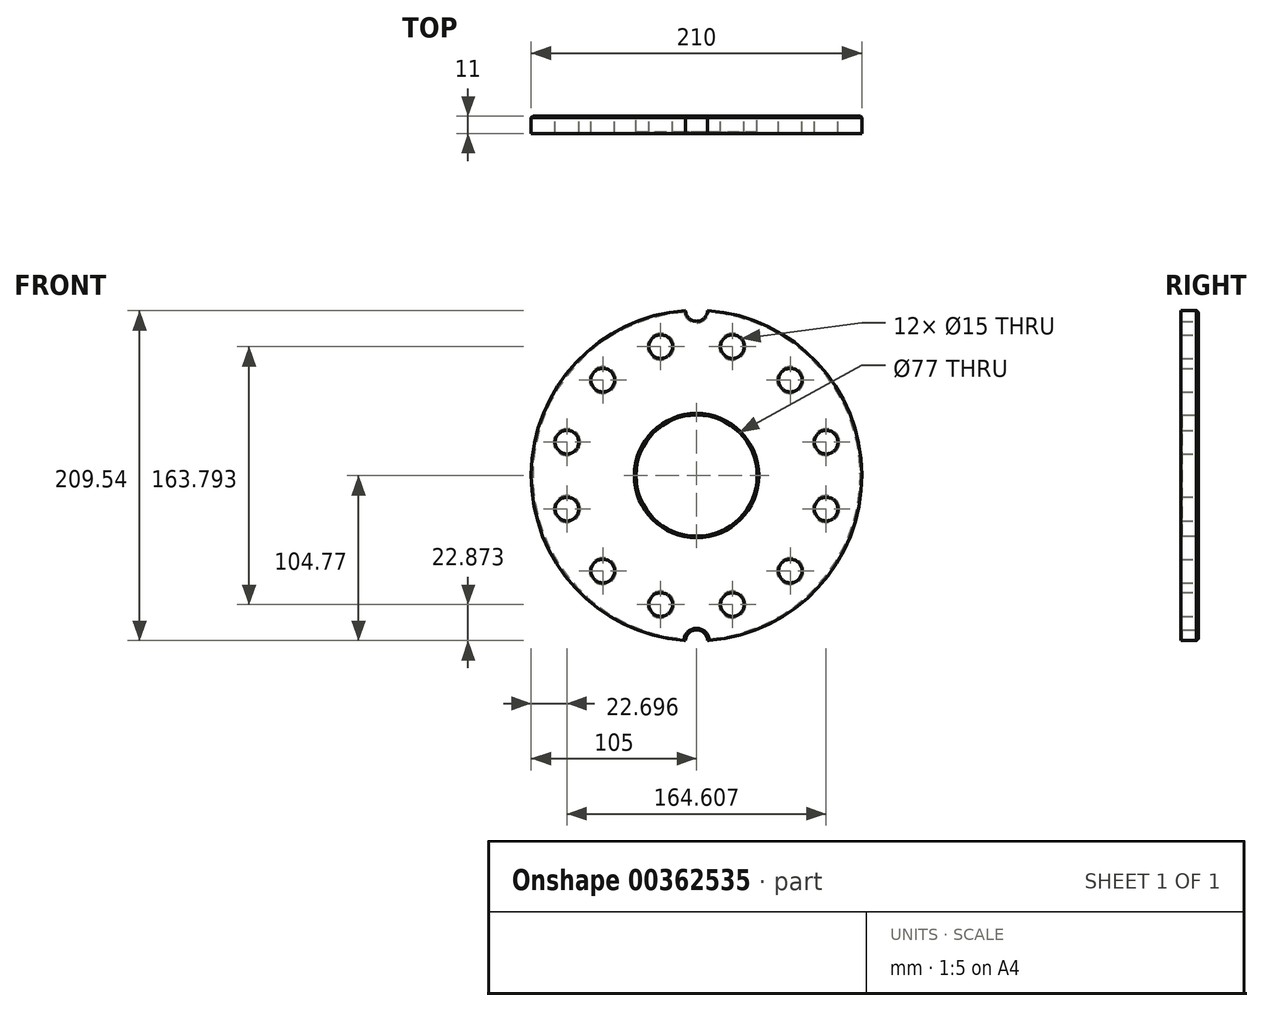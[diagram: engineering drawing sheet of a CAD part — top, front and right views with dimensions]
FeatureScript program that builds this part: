
annotation { "Feature Type Name" : "Feature", "Feature Type Description" : "" }
export const myFeature = defineFeature(function(context is Context, id is Id, definition is map)
    precondition{}
    {
        {
            var Q0;
            Q0=qCreatedBy(makeId("Front.planeOp"),FACE);
            var sketch = newSketch(context, id + "F0", { "sketchPlane" : qUnion([Q0])});
            skArc(sketch, "E0", {"start": v(-7, 104.77) * mm, "mid": v(-105, 0) * mm, "end": v(-7, -104.77) * mm});
            skCircle(sketch, "E1", {"center": v(0, 0) * mm, "radius": 38.5 * mm});
            skLineSegment(sketch, "E2", {"start": v(0, 0) * mm, "end": v(-22.76, 81.9) * mm});
            skLineSegment(sketch, "E3", {"start": v(0, 0) * mm, "end": v(22.76, 81.9) * mm});
            skCircle(sketch, "E4", {"center": v(-22.76, 81.9) * mm, "radius": 7.5 * mm});
            skCircle(sketch, "E5.1.0", {"center": v(-82.3, 21.24) * mm, "radius": 7.5 * mm});
            skCircle(sketch, "E5.2.0", {"center": v(-59.55, -60.66) * mm, "radius": 7.5 * mm});
            skCircle(sketch, "E5.3.0", {"center": v(22.76, -81.9) * mm, "radius": 7.5 * mm});
            skCircle(sketch, "E5.4.0", {"center": v(82.3, -21.24) * mm, "radius": 7.5 * mm});
            skCircle(sketch, "E5.5.0", {"center": v(59.55, 60.66) * mm, "radius": 7.5 * mm});
            skCircle(sketch, "E6", {"center": v(22.76, 81.9) * mm, "radius": 7.5 * mm});
            skCircle(sketch, "E7.1.0", {"center": v(-59.55, 60.66) * mm, "radius": 7.5 * mm});
            skCircle(sketch, "E7.2.0", {"center": v(-82.3, -21.24) * mm, "radius": 7.5 * mm});
            skCircle(sketch, "E7.3.0", {"center": v(-22.76, -81.9) * mm, "radius": 7.5 * mm});
            skCircle(sketch, "E7.4.0", {"center": v(59.55, -60.66) * mm, "radius": 7.5 * mm});
            skCircle(sketch, "E7.5.0", {"center": v(82.3, 21.24) * mm, "radius": 7.5 * mm});
            skArc(sketch, "E8", {"start": v(-7, 104.77) * mm, "mid": v(0, 98) * mm, "end": v(7, 104.77) * mm});
            skArc(sketch, "E9", {"start": v(7, -104.77) * mm, "mid": v(0, -98) * mm, "end": v(-7, -104.77) * mm});
            skArc(sketch, "E10.trimOffspring", {"start": v(7, -104.77) * mm, "mid": v(105, 0) * mm, "end": v(7, 104.77) * mm});
            skSolve(sketch);
        }
        {
            var Q0;
            Q0=makeQuery(id+"F0.imprint","IMPRINT",FACE,{"disambiguationData":[TD([[makeQuery(id+"F0.imprint","IMPRINT",EDGE,{"derivedFrom":sQuery(id+"F0.wireOp",EDGE,"E0")}),1.0]])]});
            extrude(context, id + "F1", {"entities" : qUnion([Q0]), "depth" : 11 * mm});
        }
        {
            var Q0;
            Q0=makeQuery(id+"F1.opExtrude","CAP_EDGE",EDGE,{"disambiguationData":[OSD([sQuery(id+"F0.wireOp",EDGE,"E1")])],"isStart":false});
            var Q1;
            Q1=makeQuery(id+"F1.opExtrude","CAP_FACE",FACE,{"disambiguationData":[OSD([sQuery(id+"F0.wireOp",EDGE,"E0"),sQuery(id+"F0.wireOp",EDGE,"E1"),sQuery(id+"F0.wireOp",EDGE,"E4"),sQuery(id+"F0.wireOp",EDGE,"E5.1.0"),sQuery(id+"F0.wireOp",EDGE,"E5.2.0"),sQuery(id+"F0.wireOp",EDGE,"E5.3.0"),sQuery(id+"F0.wireOp",EDGE,"E5.4.0"),sQuery(id+"F0.wireOp",EDGE,"E5.5.0"),sQuery(id+"F0.wireOp",EDGE,"E6"),sQuery(id+"F0.wireOp",EDGE,"E7.1.0"),sQuery(id+"F0.wireOp",EDGE,"E7.2.0"),sQuery(id+"F0.wireOp",EDGE,"E7.3.0"),sQuery(id+"F0.wireOp",EDGE,"E7.4.0"),sQuery(id+"F0.wireOp",EDGE,"E7.5.0")])],"isStart":true});
            var Q2;
            Q2=makeQuery(id+"F1.opExtrude","CAP_EDGE",EDGE,{"disambiguationData":[OSD([sQuery(id+"F0.wireOp",EDGE,"E8")])],"isStart":true});
            var Q3;
            Q3=makeQuery(id+"F1.opExtrude","CAP_EDGE",EDGE,{"disambiguationData":[OSD([sQuery(id+"F0.wireOp",EDGE,"E9")])],"isStart":true});
            var Q4;
            Q4=makeQuery(id+"F1.opExtrude","CAP_EDGE",EDGE,{"disambiguationData":[OSD([sQuery(id+"F0.wireOp",EDGE,"E9")])],"isStart":false});
            chamfer(context, id + "F2", {"entities" : qUnion([Q0, Q1, Q2, Q3, Q4]), "chamferType" : ChamferType.OFFSET_ANGLE, "width" : 1 * mm, "oppositeDirection" : false, "angle" : 45 * degree, "tangentPropagation" : true});
        }
    });
